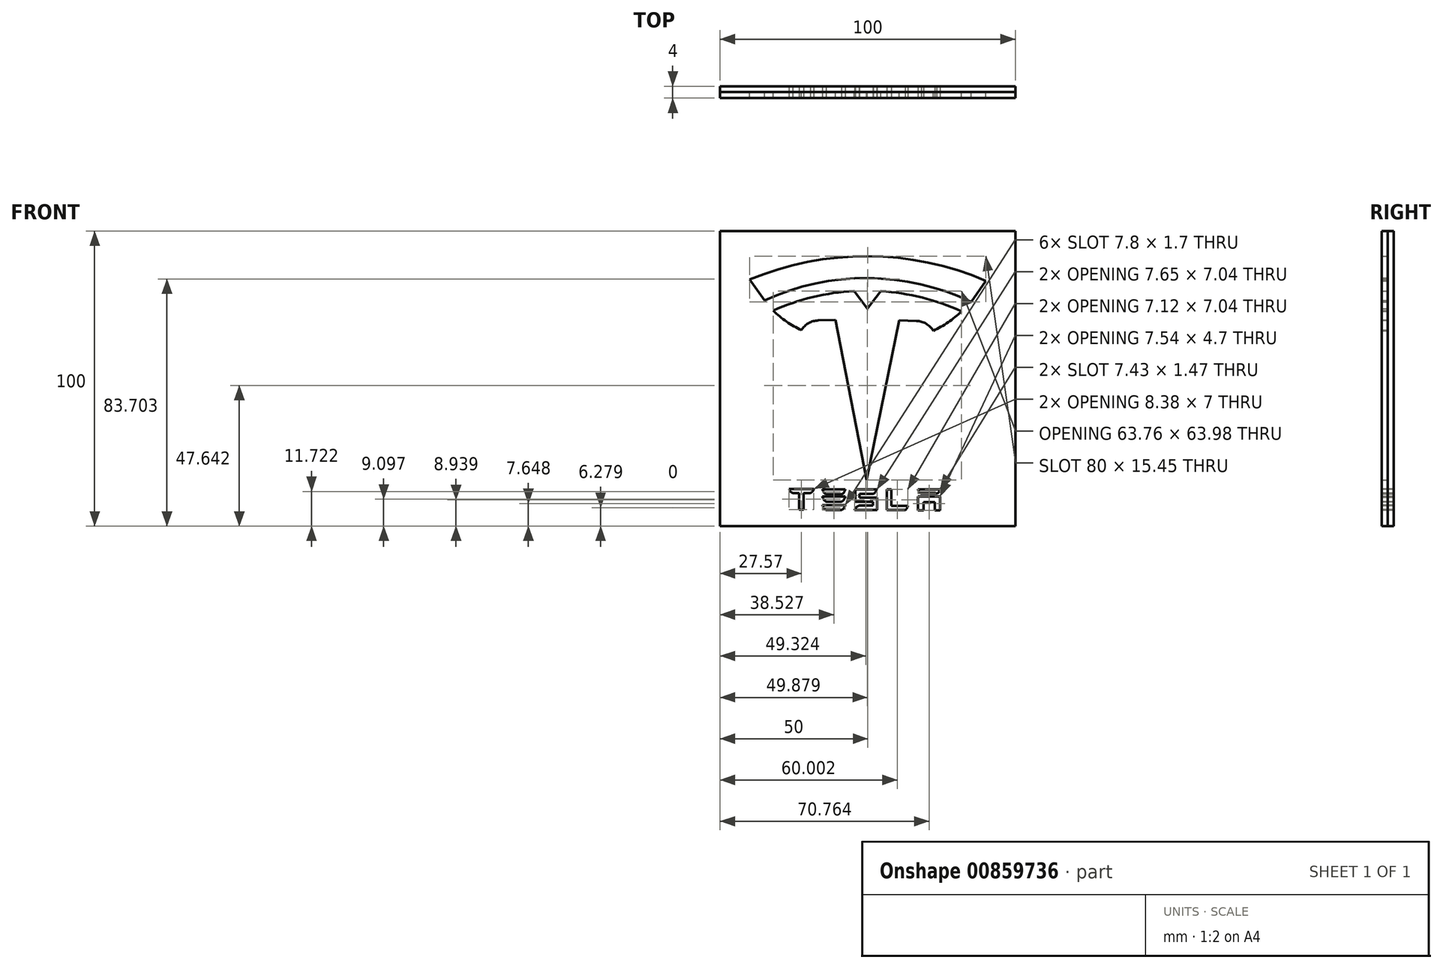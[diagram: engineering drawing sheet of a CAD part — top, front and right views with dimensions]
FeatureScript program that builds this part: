
annotation { "Feature Type Name" : "Feature", "Feature Type Description" : "" }
export const myFeature = defineFeature(function(context is Context, id is Id, definition is map)
    precondition{}
    {
        {
            var Q0;
            Q0=qCreatedBy(makeId("Front.planeOp"),FACE);
            var sketch = newSketch(context, id + "F0", { "sketchPlane" : qUnion([Q0])});
            skLineSegment(sketch, "E0.rect.bottom", {"start": v(50, 50) * mm, "end": v(-50, 50) * mm});
            skLineSegment(sketch, "E0.rect.top", {"start": v(50, -50) * mm, "end": v(-50, -50) * mm});
            skLineSegment(sketch, "E0.rect.left", {"start": v(50, 50) * mm, "end": v(50, -50) * mm});
            skLineSegment(sketch, "E0.rect.right", {"start": v(-50, 50) * mm, "end": v(-50, -50) * mm});
            skPoint(sketch, "E0.rect.middle", {"position": v(0, 0) * mm});
            skSolve(sketch);
        }
        {
            var Q0;
            Q0=makeQuery(id+"F0.imprint","IMPRINT",FACE,{"disambiguationData":[TD([[makeQuery(id+"F0.imprint","IMPRINT",EDGE,{"derivedFrom":sQuery(id+"F0.wireOp",EDGE,"E0.rect.bottom")}),1.0]])]});
            extrude(context, id + "F1", {"entities" : qUnion([Q0]), "offsetDistance" : 25 * mm, "depth" : 2 * mm});
        }
        {
            var Q0;
            Q0=makeQuery(id+"F1.opExtrude","CAP_FACE",FACE,{"disambiguationData":[OSD([sQuery(id+"F0.wireOp",EDGE,"E0.rect.bottom"),sQuery(id+"F0.wireOp",EDGE,"E0.rect.top"),sQuery(id+"F0.wireOp",EDGE,"E0.rect.left"),sQuery(id+"F0.wireOp",EDGE,"E0.rect.right")])],"isStart":false});
            var sketch = newSketch(context, id + "F2", { "sketchPlane" : qUnion([Q0])});
            skArc(sketch, "E1", {"start": v(40, 33.1) * mm, "mid": v(0.04, 41.43) * mm, "end": v(-40, 33.52) * mm});
            skArc(sketch, "E2", {"start": v(35, 25.98) * mm, "mid": v(0.05, 34.02) * mm, "end": v(-35, 26.39) * mm});
            skLineSegment(sketch, "E3", {"start": v(0, 50) * mm, "end": v(-0.44, -48.04) * mm, "construction": true});
            skLineSegment(sketch, "E4", {"start": v(35, 25.98) * mm, "end": v(40, 33.1) * mm});
            skLineSegment(sketch, "E5", {"start": v(-35, 26.39) * mm, "end": v(-40, 33.52) * mm});
            skArc(sketch, "E6", {"start": v(32, 22.62) * mm, "mid": v(31.87, 22.68) * mm, "end": v(31.75, 22.74) * mm});
            skArc(sketch, "E7", {"start": v(-32, 23.03) * mm, "mid": v(-27.53, 19.3) * mm, "end": v(-22.5, 16.38) * mm});
            skArc(sketch, "E8.MirrorCS", {"start": v(31.76, 22.75) * mm, "mid": v(27.26, 19.05) * mm, "end": v(22.2, 16.18) * mm});
            skArc(sketch, "E9.trimOffspring", {"start": v(-4.58, 29.63) * mm, "mid": v(-18.6, 27.59) * mm, "end": v(-32, 23.03) * mm});
            skArc(sketch, "E10.MirrorCS", {"start": v(4.4, 29.6) * mm, "mid": v(18.4, 27.42) * mm, "end": v(31.76, 22.75) * mm});
            skArc(sketch, "E11", {"start": v(-16.74, 19.67) * mm, "mid": v(-20.03, 18.75) * mm, "end": v(-22.5, 16.38) * mm});
            skLineSegment(sketch, "E12", {"start": v(-16.74, 19.67) * mm, "end": v(-10.89, 19.82) * mm});
            skLineSegment(sketch, "E13", {"start": v(-10.89, 19.82) * mm, "end": v(-0.38, -34.35) * mm});
            skArc(sketch, "E14.MirrorCS", {"start": v(16.47, 19.52) * mm, "mid": v(19.75, 18.57) * mm, "end": v(22.2, 16.18) * mm});
            skLineSegment(sketch, "E15.MirrorCS", {"start": v(16.47, 19.52) * mm, "end": v(10.62, 19.72) * mm});
            skLineSegment(sketch, "E16.MirrorCS", {"start": v(10.62, 19.72) * mm, "end": v(-0.38, -34.35) * mm});
            skLineSegment(sketch, "E17", {"start": v(-4.58, 29.63) * mm, "end": v(-0.12, 23.62) * mm});
            skLineSegment(sketch, "E18.MirrorCS", {"start": v(4.4, 29.6) * mm, "end": v(-0.12, 23.62) * mm});
            skPoint(sketch, "E19.orphan", {"position": v(-0.1, 29.74) * mm});
            skSolve(sketch);
        }
        {
            var Q0;
            Q0=makeQuery(id+"F2.imprint","IMPRINT",FACE,{"disambiguationData":[TD([[makeQuery(id+"F2.imprint","IMPRINT",EDGE,{"derivedFrom":sQuery(id+"F2.wireOp",EDGE,"E1")}),-1.0]])]});
            extrude(context, id + "F3", {"entities" : qUnion([Q0]), "offsetDistance" : 25 * mm, "depth" : 2 * mm});
        }
        {
            var Q0;
            Q0=makeQuery(id+"F3.opExtrude","CAP_FACE",FACE,{"disambiguationData":[OSD([sQuery(id+"F0.wireOp",EDGE,"E0.rect.bottom"),sQuery(id+"F0.wireOp",EDGE,"E0.rect.top"),sQuery(id+"F0.wireOp",EDGE,"E0.rect.left"),sQuery(id+"F0.wireOp",EDGE,"E0.rect.right"),sQuery(id+"F2.wireOp",EDGE,"E1"),sQuery(id+"F2.wireOp",EDGE,"E2"),sQuery(id+"F2.wireOp",EDGE,"E4"),sQuery(id+"F2.wireOp",EDGE,"E5"),sQuery(id+"F2.wireOp",EDGE,"E7"),sQuery(id+"F2.wireOp",EDGE,"E8.MirrorCS"),sQuery(id+"F2.wireOp",EDGE,"E9.trimOffspring"),sQuery(id+"F2.wireOp",EDGE,"E10.MirrorCS"),sQuery(id+"F2.wireOp",EDGE,"E11"),sQuery(id+"F2.wireOp",EDGE,"E12"),sQuery(id+"F2.wireOp",EDGE,"E13"),sQuery(id+"F2.wireOp",EDGE,"E14.MirrorCS"),sQuery(id+"F2.wireOp",EDGE,"E15.MirrorCS"),sQuery(id+"F2.wireOp",EDGE,"E16.MirrorCS"),sQuery(id+"F2.wireOp",EDGE,"E17"),sQuery(id+"F2.wireOp",EDGE,"E18.MirrorCS")])],"isStart":false});
            var sketch = newSketch(context, id + "F4", { "sketchPlane" : qUnion([Q0])});
            skLineSegment(sketch, "E20", {"start": v(-26.62, -37.4) * mm, "end": v(-18.24, -37.4) * mm});
            skArc(sketch, "E21", {"start": v(-26.62, -37.4) * mm, "mid": v(-26.2, -38.25) * mm, "end": v(-25.42, -38.82) * mm});
            skLineSegment(sketch, "E22", {"start": v(-22.43, -37.4) * mm, "end": v(-22.43, -44.4) * mm, "construction": true});
            skArc(sketch, "E23.MirrorCS", {"start": v(-18.24, -37.4) * mm, "mid": v(-18.67, -38.25) * mm, "end": v(-19.44, -38.82) * mm});
            skLineSegment(sketch, "E24", {"start": v(-25.42, -38.82) * mm, "end": v(-23.2, -38.82) * mm});
            skLineSegment(sketch, "E25", {"start": v(-23.2, -38.82) * mm, "end": v(-23.2, -44.4) * mm});
            skLineSegment(sketch, "E26", {"start": v(-23.2, -44.4) * mm, "end": v(-22.43, -44.4) * mm});
            skLineSegment(sketch, "E27.MirrorCS", {"start": v(-19.44, -38.82) * mm, "end": v(-21.67, -38.82) * mm});
            skLineSegment(sketch, "E28.MirrorCS", {"start": v(-21.67, -38.82) * mm, "end": v(-21.67, -44.4) * mm});
            skLineSegment(sketch, "E29.MirrorCS", {"start": v(-21.67, -44.4) * mm, "end": v(-22.43, -44.4) * mm});
            skLineSegment(sketch, "E30", {"start": v(-15.37, -37.56) * mm, "end": v(-11.47, -37.56) * mm});
            skArc(sketch, "E31", {"start": v(-15.37, -37.56) * mm, "mid": v(-14.9, -38.54) * mm, "end": v(-14.09, -39.26) * mm});
            skLineSegment(sketch, "E32", {"start": v(-11.47, -37.56) * mm, "end": v(-11.47, -45.21) * mm, "construction": true});
            skLineSegment(sketch, "E33", {"start": v(-14.09, -39.26) * mm, "end": v(-11.47, -39.26) * mm});
            skLineSegment(sketch, "E34", {"start": v(-15.37, -40.03) * mm, "end": v(-11.47, -40.03) * mm});
            skArc(sketch, "E35", {"start": v(-15.37, -40.03) * mm, "mid": v(-14.9, -41.01) * mm, "end": v(-14.09, -41.73) * mm});
            skLineSegment(sketch, "E36", {"start": v(-14.09, -41.73) * mm, "end": v(-11.47, -41.73) * mm});
            skLineSegment(sketch, "E37", {"start": v(-15.37, -42.87) * mm, "end": v(-11.47, -42.87) * mm});
            skArc(sketch, "E38", {"start": v(-15.37, -42.87) * mm, "mid": v(-14.9, -43.85) * mm, "end": v(-14.09, -44.57) * mm});
            skLineSegment(sketch, "E39", {"start": v(-14.09, -44.57) * mm, "end": v(-11.47, -44.57) * mm});
            skArc(sketch, "E40.MirrorCS", {"start": v(-7.57, -37.56) * mm, "mid": v(-8.05, -38.54) * mm, "end": v(-8.86, -39.26) * mm});
            skLineSegment(sketch, "E41.MirrorCS", {"start": v(-8.86, -39.26) * mm, "end": v(-11.47, -39.26) * mm});
            skLineSegment(sketch, "E42.MirrorCS", {"start": v(-7.57, -40.03) * mm, "end": v(-11.47, -40.03) * mm});
            skArc(sketch, "E43.MirrorCS", {"start": v(-7.57, -40.03) * mm, "mid": v(-8.05, -41.01) * mm, "end": v(-8.86, -41.73) * mm});
            skLineSegment(sketch, "E44.MirrorCS", {"start": v(-8.86, -41.73) * mm, "end": v(-11.47, -41.73) * mm});
            skLineSegment(sketch, "E45.MirrorCS", {"start": v(-7.57, -42.87) * mm, "end": v(-11.47, -42.87) * mm});
            skArc(sketch, "E46.MirrorCS", {"start": v(-7.57, -42.87) * mm, "mid": v(-8.05, -43.85) * mm, "end": v(-8.86, -44.57) * mm});
            skLineSegment(sketch, "E47.MirrorCS", {"start": v(-8.86, -44.57) * mm, "end": v(-11.47, -44.57) * mm});
            skLineSegment(sketch, "E48", {"start": v(3.06, -37.54) * mm, "end": v(-4.19, -37.54) * mm});
            skLineSegment(sketch, "E49", {"start": v(-4.19, -37.54) * mm, "end": v(-4.19, -41.7) * mm});
            skLineSegment(sketch, "E50", {"start": v(-4.19, -41.7) * mm, "end": v(1.75, -41.7) * mm});
            skLineSegment(sketch, "E51", {"start": v(1.75, -41.7) * mm, "end": v(1.75, -43.05) * mm});
            skLineSegment(sketch, "E52", {"start": v(1.75, -43.05) * mm, "end": v(-2.97, -43.05) * mm});
            skArc(sketch, "E53", {"start": v(-2.97, -43.05) * mm, "mid": v(-3.89, -43.67) * mm, "end": v(-4.5, -44.58) * mm});
            skLineSegment(sketch, "E54", {"start": v(-4.5, -44.58) * mm, "end": v(3.15, -44.58) * mm});
            skLineSegment(sketch, "E55", {"start": v(3.15, -44.58) * mm, "end": v(3.15, -40.42) * mm});
            skLineSegment(sketch, "E56", {"start": v(3.15, -40.42) * mm, "end": v(-2.79, -40.42) * mm});
            skLineSegment(sketch, "E57", {"start": v(-2.79, -40.42) * mm, "end": v(-2.79, -39.07) * mm});
            skLineSegment(sketch, "E58", {"start": v(-2.79, -39.07) * mm, "end": v(1.93, -39.07) * mm});
            skArc(sketch, "E59", {"start": v(1.93, -39.07) * mm, "mid": v(2.63, -38.4) * mm, "end": v(3.06, -37.54) * mm});
            skPoint(sketch, "E60.orphan", {"position": v(-7.57, -37.56) * mm});
            skLineSegment(sketch, "E61", {"start": v(-11.47, -37.56) * mm, "end": v(-7.57, -37.56) * mm});
            skLineSegment(sketch, "E62", {"start": v(6.44, -37.54) * mm, "end": v(6.44, -44.58) * mm});
            skLineSegment(sketch, "E63", {"start": v(6.44, -44.58) * mm, "end": v(12.74, -44.58) * mm});
            skLineSegment(sketch, "E64", {"start": v(6.44, -37.54) * mm, "end": v(7.93, -37.54) * mm});
            skLineSegment(sketch, "E65", {"start": v(7.93, -37.54) * mm, "end": v(7.93, -43.2) * mm});
            skLineSegment(sketch, "E66", {"start": v(7.93, -43.2) * mm, "end": v(13.56, -43.2) * mm});
            skArc(sketch, "E67", {"start": v(12.74, -44.58) * mm, "mid": v(13.28, -43.97) * mm, "end": v(13.56, -43.2) * mm});
            skLineSegment(sketch, "E68", {"start": v(20.76, -37.5) * mm, "end": v(20.76, -45.16) * mm, "construction": true});
            skLineSegment(sketch, "E69", {"start": v(17.05, -37.54) * mm, "end": v(20.76, -37.54) * mm});
            skArc(sketch, "E70", {"start": v(17.05, -37.54) * mm, "mid": v(17.4, -38.43) * mm, "end": v(18.15, -39.01) * mm});
            skLineSegment(sketch, "E71", {"start": v(18.15, -39.01) * mm, "end": v(20.76, -39.01) * mm});
            skLineSegment(sketch, "E72", {"start": v(20.76, -40) * mm, "end": v(17, -40) * mm});
            skLineSegment(sketch, "E73", {"start": v(17, -40) * mm, "end": v(17, -44.7) * mm});
            skLineSegment(sketch, "E74", {"start": v(17, -44.7) * mm, "end": v(18.86, -44.7) * mm});
            skLineSegment(sketch, "E75", {"start": v(18.86, -44.7) * mm, "end": v(18.86, -41.85) * mm});
            skLineSegment(sketch, "E76", {"start": v(18.86, -41.85) * mm, "end": v(20.76, -41.85) * mm});
            skLineSegment(sketch, "E77.MirrorCS", {"start": v(24.48, -37.54) * mm, "end": v(20.76, -37.54) * mm});
            skArc(sketch, "E78.MirrorCS", {"start": v(24.48, -37.54) * mm, "mid": v(24.13, -38.43) * mm, "end": v(23.38, -39.01) * mm});
            skLineSegment(sketch, "E79.MirrorCS", {"start": v(23.38, -39.01) * mm, "end": v(20.76, -39.01) * mm});
            skLineSegment(sketch, "E80.MirrorCS", {"start": v(20.76, -40) * mm, "end": v(24.53, -40) * mm});
            skLineSegment(sketch, "E81.MirrorCS", {"start": v(24.53, -40) * mm, "end": v(24.53, -44.7) * mm});
            skLineSegment(sketch, "E82.MirrorCS", {"start": v(24.53, -44.7) * mm, "end": v(22.67, -44.7) * mm});
            skLineSegment(sketch, "E83.MirrorCS", {"start": v(22.67, -44.7) * mm, "end": v(22.67, -41.85) * mm});
            skLineSegment(sketch, "E84.MirrorCS", {"start": v(22.67, -41.85) * mm, "end": v(20.76, -41.85) * mm});
            skSolve(sketch);
        }
        {
            var Q0;
            Q0=makeQuery(id+"F4.imprint","IMPRINT",FACE,{"disambiguationData":[TD([[makeQuery(id+"F4.imprint","IMPRINT",EDGE,{"derivedFrom":sQuery(id+"F4.wireOp",EDGE,"E20")}),-1.0]])]});
            var Q1;
            Q1=makeQuery(id+"F4.imprint","IMPRINT",FACE,{"disambiguationData":[TD([[makeQuery(id+"F4.imprint","IMPRINT",EDGE,{"derivedFrom":sQuery(id+"F4.wireOp",EDGE,"E30")}),-1.0]])]});
            var Q2;
            Q2=makeQuery(id+"F4.imprint","IMPRINT",FACE,{"disambiguationData":[TD([[makeQuery(id+"F4.imprint","IMPRINT",EDGE,{"derivedFrom":sQuery(id+"F4.wireOp",EDGE,"E34")}),-1.0]])]});
            var Q3;
            Q3=makeQuery(id+"F4.imprint","IMPRINT",FACE,{"disambiguationData":[TD([[makeQuery(id+"F4.imprint","IMPRINT",EDGE,{"derivedFrom":sQuery(id+"F4.wireOp",EDGE,"E37")}),-1.0]])]});
            var Q4;
            Q4=makeQuery(id+"F4.imprint","IMPRINT",FACE,{"disambiguationData":[TD([[makeQuery(id+"F4.imprint","IMPRINT",EDGE,{"derivedFrom":sQuery(id+"F4.wireOp",EDGE,"E48")}),1.0]])]});
            var Q5;
            Q5=makeQuery(id+"F4.imprint","IMPRINT",FACE,{"disambiguationData":[TD([[makeQuery(id+"F4.imprint","IMPRINT",EDGE,{"derivedFrom":sQuery(id+"F4.wireOp",EDGE,"E62")}),1.0]])]});
            var Q6;
            Q6=makeQuery(id+"F4.imprint","IMPRINT",FACE,{"disambiguationData":[TD([[makeQuery(id+"F4.imprint","IMPRINT",EDGE,{"derivedFrom":sQuery(id+"F4.wireOp",EDGE,"E72")}),1.0]])]});
            var Q7;
            Q7=makeQuery(id+"F4.imprint","IMPRINT",FACE,{"disambiguationData":[TD([[makeQuery(id+"F4.imprint","IMPRINT",EDGE,{"derivedFrom":sQuery(id+"F4.wireOp",EDGE,"E69")}),-1.0]])]});
            extrude(context, id + "F5", {"entities" : qUnion([Q0, Q1, Q2, Q3, Q4, Q5, Q6, Q7]), "operationType" : NewBodyOperationType.REMOVE, "oppositeDirection" : true, "depth" : 10 * mm});
        }
    });
